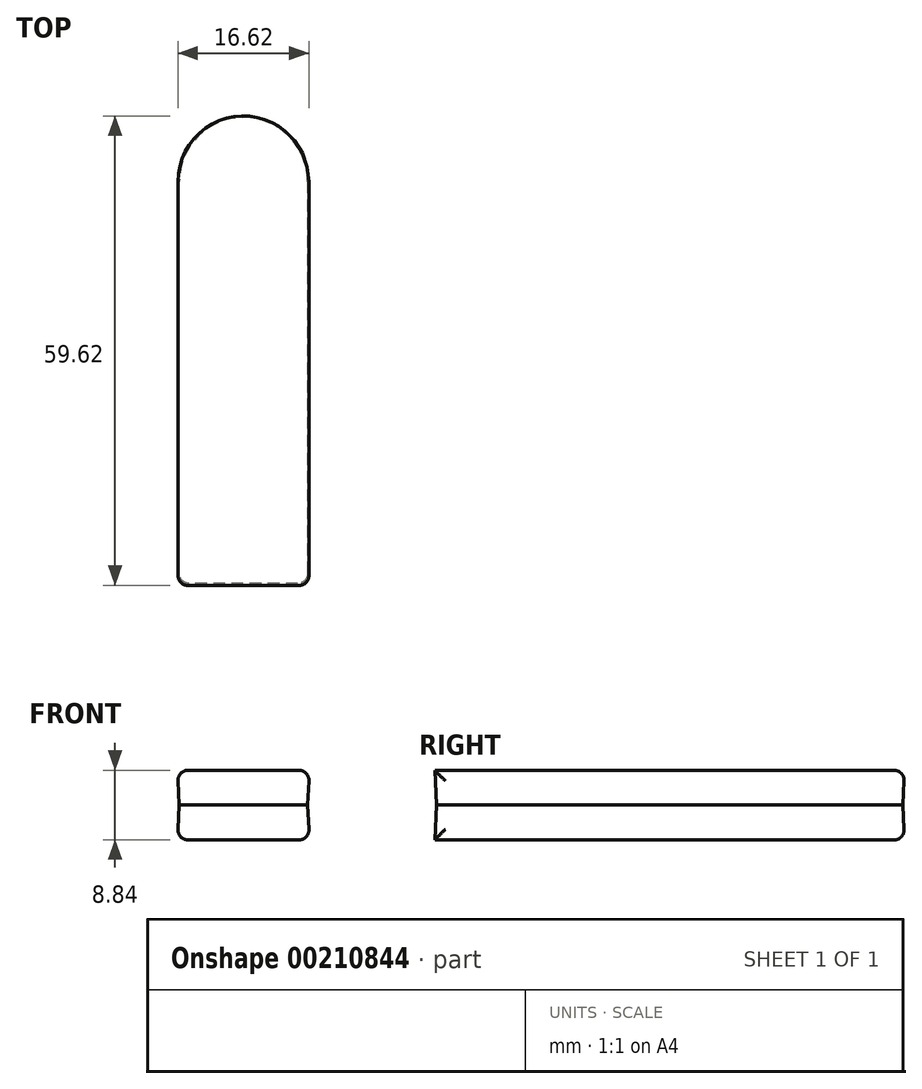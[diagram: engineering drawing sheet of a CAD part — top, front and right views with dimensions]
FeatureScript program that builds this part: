
annotation { "Feature Type Name" : "Feature", "Feature Type Description" : "" }
export const myFeature = defineFeature(function(context is Context, id is Id, definition is map)
    precondition{}
    {
        {
            var Q0;
            Q0=qCreatedBy(makeId("Top.planeOp"),FACE);
            var sketch = newSketch(context, id + "F0", { "sketchPlane" : qUnion([Q0])});
            skLineSegment(sketch, "E0", {"start": v(-8.15, 77.21) * mm, "end": v(-8.15, 26.14) * mm});
            skLineSegment(sketch, "E1", {"start": v(-8.15, 26.14) * mm, "end": v(8.15, 26.14) * mm});
            skLineSegment(sketch, "E2", {"start": v(0, 0) * mm, "end": v(0, 78.16) * mm});
            skLineSegment(sketch, "E3.MirrorCS", {"start": v(8.15, 77.21) * mm, "end": v(8.15, 26.14) * mm});
            skLineSegment(sketch, "E4.MirrorCS", {"start": v(8.15, 26.14) * mm, "end": v(-8.15, 26.14) * mm});
            skPoint(sketch, "E5.orphan", {"position": v(-5.1, 26.14) * mm});
            skPoint(sketch, "E6.orphan", {"position": v(5.1, 26.14) * mm});
            skArc(sketch, "E7", {"start": v(8.15, 77.21) * mm, "mid": v(0, 85.36) * mm, "end": v(-8.15, 77.21) * mm});
            skSolve(sketch);
        }
        {
            var Q0;
            Q0 = qSketchRegion(id + "F0", true);
            extrude(context, id + "F1", {"entities" : qUnion([Q0]), "endBound" : BoundingType.SYMMETRIC, "depth" : 8.85 * mm, "hasDraft" : true, "draftAngle" : 3 * degree, "hasSecondDirection" : true, "secondDirectionOppositeDirection" : false, "secondDirectionDepth" : 8.84 * mm});
        }
        {
            var Q0;
            Q0=makeQuery(id+"F1.opExtrude","CAP_EDGE",EDGE,{"disambiguationData":[OSD([sQuery(id+"F0.wireOp",EDGE,"E0")])],"isStart":false});
            var Q1;
            Q1=makeQuery(id+"F1.opExtrude","CAP_EDGE",EDGE,{"disambiguationData":[OSD([sQuery(id+"F0.wireOp",EDGE,"E0")])],"isStart":true});
            var Q2;
            Q2=makeQuery(id+"F1.opExtrude","SWEPT_EDGE",EDGE,{"disambiguationData":[OSD([sQuery(id+"F0.wireOp",EDGE,"E0"),sQuery(id+"F0.wireOp",EDGE,"E4.MirrorCS")])]});
            var Q3;
            Q3=makeQuery(id+"F1.opExtrude","CAP_EDGE",EDGE,{"disambiguationData":[OSD([sQuery(id+"F0.wireOp",EDGE,"E4.MirrorCS")])],"isStart":false});
            var Q4;
            Q4=makeQuery(id+"F1.opExtrude","CAP_EDGE",EDGE,{"disambiguationData":[OSD([sQuery(id+"F0.wireOp",EDGE,"E4.MirrorCS")])],"isStart":true});
            var Q5;
            Q5=makeQuery(id+"F1.opExtrude","SWEPT_EDGE",EDGE,{"disambiguationData":[OSD([sQuery(id+"F0.wireOp",EDGE,"E3.MirrorCS"),sQuery(id+"F0.wireOp",EDGE,"E4.MirrorCS")])]});
            fillet(context, id + "F2", {"entities" : qUnion([Q0, Q1, Q2, Q3, Q4, Q5]), "radius" : 1.27 * mm, "tangentPropagation" : true, "allowEdgeOverflow" : false});
        }
    });
